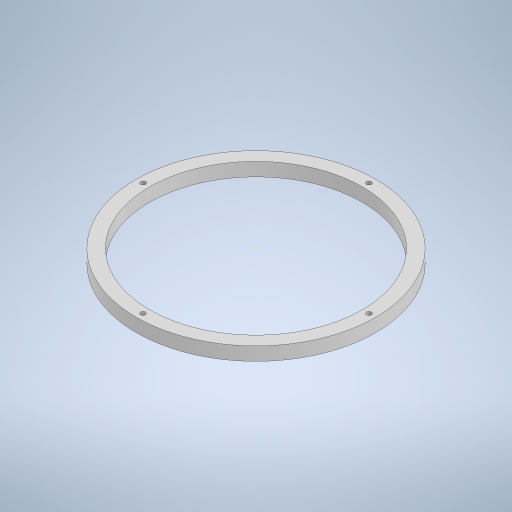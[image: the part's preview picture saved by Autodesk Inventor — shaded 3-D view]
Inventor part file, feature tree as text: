
AUTODESK INVENTOR PART (.ipt)
format: ipt  version: 2023 (Build 270158000, 158)  size: 254,464 bytes
history: native  units: in
note: dims shown in document units (in); Inventor stores cm internally (conversion verified against a paired STEP export)
features: sketch x3, extrude x1, hole x1, pattern_circular x1
ambient origin geometry x8: Origin, YZ Plane, XZ Plane, XY Plane, X Axis, Y Axis, Z Axis, Center Point
bodies: Solid1 (feature_tree)
feature tree (6):
  extrude  "Extrusion1"  Depth=8.7598in
  hole  "Hole1"  [1 undecoded]
  pattern_circular  "Circular Pattern1"  Count=4 Angle=360.0deg
  sketch  "Sketch3"  dims[d6=0.1969in d7=0.2362in d8=0.1969in d9=0.0787in d10=90.0deg d11=0.315in d12=0.8108in d13=1.5748in d14=360.0deg]
  sketch  "Sketch1"  dims[d0=9.8425in d1=8.7598in]
  sketch  "Sketch2"  dims[d2=0.5512in d3=0.0in d4=9.3012in]
note: 1 required parameter value undecoded (feature->parameter linkage not recoverable at this tier; creation-order binding heuristic only, values carry confidence <= 0.55)
